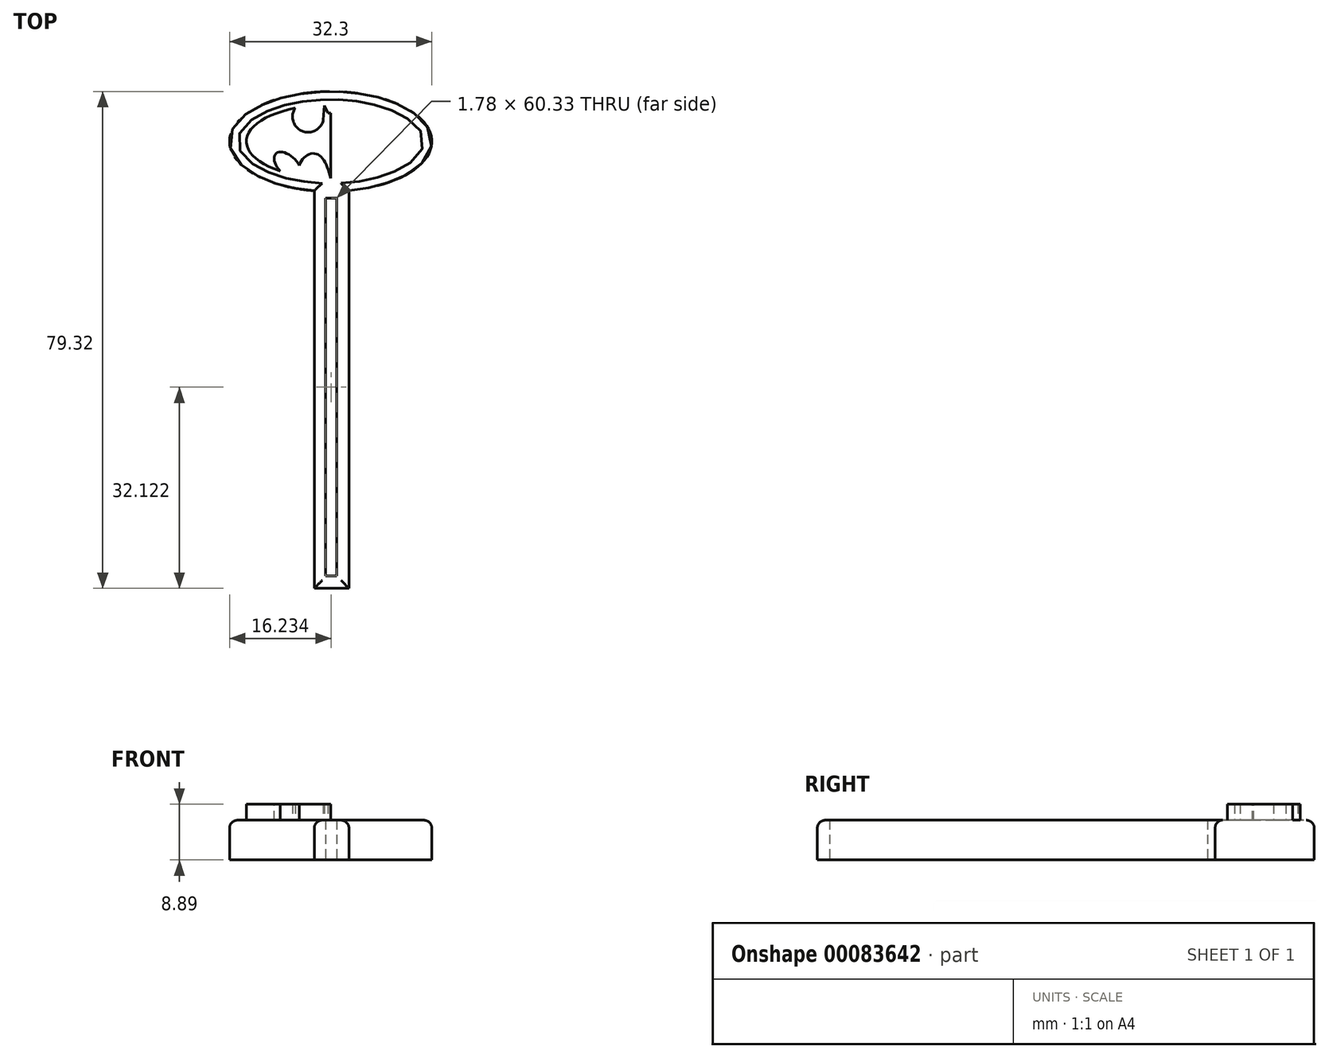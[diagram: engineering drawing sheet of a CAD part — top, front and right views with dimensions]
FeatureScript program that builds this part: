
annotation { "Feature Type Name" : "Feature", "Feature Type Description" : "" }
export const myFeature = defineFeature(function(context is Context, id is Id, definition is map)
    precondition{}
    {
        {
            var Q0;
            Q0=qCreatedBy(makeId("Top.planeOp"),FACE);
            var sketch = newSketch(context, id + "F0", { "sketchPlane" : qUnion([Q0])});
            skLineSegment(sketch, "E0.bottom", {"start": v(-8.05, 29.3) * mm, "end": v(-6.28, 29.3) * mm});
            skLineSegment(sketch, "E0.top", {"start": v(-8.05, -31.02) * mm, "end": v(-6.28, -31.02) * mm});
            skLineSegment(sketch, "E0.left", {"start": v(-8.05, 29.3) * mm, "end": v(-8.05, -31.02) * mm});
            skLineSegment(sketch, "E0.right", {"start": v(-6.28, 29.3) * mm, "end": v(-6.28, -31.02) * mm});
            skLineSegment(sketch, "E1.top", {"start": v(-9.87, -32.98) * mm, "end": v(-4.33, -32.98) * mm});
            skLineSegment(sketch, "E1.left", {"start": v(-9.87, 30.52) * mm, "end": v(-9.87, -32.98) * mm});
            skLineSegment(sketch, "E1.right", {"start": v(-4.33, 30.52) * mm, "end": v(-4.33, -32.98) * mm});
            skEllipticalArc(sketch, "E2", {});
            skPoint(sketch, "E3.startSnap0", {"position": v(-7.25, 46.34) * mm});
            skPoint(sketch, "E3.start.orphan", {"position": v(-7.25, 51.5) * mm});
            const initialGuessF0  = {"E2": [-0.007252356503158808, 0.03836836293339729, 1, 0, 0.016150043811649084, 0.007975973144719452, 4.894343702648654, 4.54976842266986]};
            skSetInitialGuess(sketch, initialGuessF0);
            skSolve(sketch);
        }
        {
            var Q0;
            Q0 = qSketchRegion(id + "F0", true);
            extrude(context, id + "F1", {"entities" : qUnion([Q0]), "depth" : 6.35 * mm});
        }
        {
            var Q0;
            Q0=makeQuery(id+"F1.opExtrude","CAP_FACE",FACE,{"disambiguationData":[OSD([sQuery(id+"F0.wireOp",EDGE,"E0.bottom"),sQuery(id+"F0.wireOp",EDGE,"E0.top"),sQuery(id+"F0.wireOp",EDGE,"E0.left"),sQuery(id+"F0.wireOp",EDGE,"E0.right"),sQuery(id+"F0.wireOp",EDGE,"E1.top"),sQuery(id+"F0.wireOp",EDGE,"E1.left"),sQuery(id+"F0.wireOp",EDGE,"E1.right"),sQuery(id+"F0.wireOp",EDGE,"E2")])],"isStart":false});
            var sketch = newSketch(context, id + "F2", { "sketchPlane" : qUnion([Q0])});
            skEllipticalArc(sketch, "E4", {});
            skLineSegment(sketch, "E5", {"start": v(-7.25, 48.68) * mm, "end": v(-7.25, 32.47) * mm});
            skPoint(sketch, "E5.endSnap0", {"position": v(-7.25, 30.4) * mm});
            skLineSegment(sketch, "E6", {"start": v(-7.25, 42.88) * mm, "end": v(-6.79, 42.88) * mm});
            skPoint(sketch, "E7.first.point", {"position": v(-5.08, 42) * mm});
            skPoint(sketch, "E7.second.point", {"position": v(-1.6, 43.72) * mm});
            skPoint(sketch, "E7.third.point", {"position": v(-3.3, 39.92) * mm});
            skEllipticalArc(sketch, "E8", {});
            skFitSpline(sketch, "E9", {"points": [v(-7.25, 32.47) * mm, v(-4.78, 36.44) * mm, v(-2.26, 34.55) * mm], "startDerivative": vector(2.36, 11.13) * mm, "endDerivative": vector(2.41, -8.56) * mm});
            skEllipticalArc(sketch, "E10.trimOffspring", {});
            skPoint(sketch, "E11.trimOffspring.end.orphan", {"position": v(-7.25, 29.75) * mm});
            skLineSegment(sketch, "E12.MirrorCS", {"start": v(-7.25, 42.88) * mm, "end": v(-7.72, 42.88) * mm});
            skEllipticalArc(sketch, "E13.MirrorCS", {});
            skFitSpline(sketch, "E14.MirrorCS", {"points": [v(-7.25, 32.47) * mm, v(-9.73, 36.44) * mm, v(-12.25, 34.55) * mm], "startDerivative": vector(-2.36, 11.13) * mm, "endDerivative": vector(-2.41, -8.56) * mm});
            skLineSegment(sketch, "E15", {"start": v(-6.79, 42.88) * mm, "end": v(-6.26, 44.13) * mm});
            skLineSegment(sketch, "E16", {"start": v(-6.26, 44.13) * mm, "end": v(-6.07, 41.8) * mm});
            skArc(sketch, "E17", {"start": v(-6.07, 41.8) * mm, "mid": v(-2.67, 40.04) * mm, "end": v(-1.6, 43.72) * mm});
            skPoint(sketch, "E17.third.point", {"position": v(-2.29, 40.25) * mm});
            skLineSegment(sketch, "E18.MirrorCS", {"start": v(-7.72, 42.88) * mm, "end": v(-8.25, 44.13) * mm});
            skLineSegment(sketch, "E19.MirrorCS", {"start": v(-8.25, 44.13) * mm, "end": v(-8.43, 41.8) * mm});
            skArc(sketch, "E20.MirrorCS", {"start": v(-8.43, 41.8) * mm, "mid": v(-11.83, 40.04) * mm, "end": v(-12.9, 43.72) * mm});
            const initialGuessF2  = {"E4": [-0.007252356503158808, 0.03836836293339729, 1, 0, 0.013452716371891214, 0.0058950630208120984, 5.355480264337791, 1.137223244960225], "E8": [-0.00042749958811327815, 0.03451338782906532, 0.7071070265716229, 0.7071065358013869, 0.002727908301320936, 0.0014921496315674547, 4.811673716025654, 2.054311453161399], "E10.trimOffspring": [-0.007252356503158808, 0.03836836293339729, 1, 0, 0.013452716371891214, 0.0058950630208120984, 2.0043694086295685, 4.069297696431589], "E13.MirrorCS": [-0.014078464221015828, 0.034509578750198666, -0.7071070265716227, 0.7071065358013872, 0.002727908301320936, 0.0014921496315674547, 4.228873854018188, 1.4715115911539325]};
            skSetInitialGuess(sketch, initialGuessF2);
            skSolve(sketch);
        }
        {
            var Q0;
            Q0 = qSketchRegion(id + "F2", true);
            extrude(context, id + "F3", {"entities" : qUnion([Q0]), "depth" : 2.54 * mm});
        }
        {
            var Q0;
            Q0=makeQuery(id+"F1.opExtrude","CAP_EDGE",EDGE,{"disambiguationData":[OSD([sQuery(id+"F0.wireOp",EDGE,"E2")])],"isStart":false});
            fillet(context, id + "F4", {"entities" : qUnion([Q0]), "radius" : 1.27 * mm, "tangentPropagation" : true, "allowEdgeOverflow" : false});
        }
        {
            var Q0;
            Q0=makeQuery(id+"F1.opExtrude","CAP_EDGE",EDGE,{"disambiguationData":[OSD([sQuery(id+"F0.wireOp",EDGE,"E1.right")])],"isStart":false});
            var Q1;
            Q1=makeQuery(id+"F1.opExtrude","CAP_EDGE",EDGE,{"disambiguationData":[OSD([sQuery(id+"F0.wireOp",EDGE,"E1.left")])],"isStart":false});
            var Q2;
            Q2=makeQuery(id+"F1.opExtrude","CAP_EDGE",EDGE,{"disambiguationData":[OSD([sQuery(id+"F0.wireOp",EDGE,"E1.top")])],"isStart":false});
            fillet(context, id + "F5", {"entities" : qUnion([Q0, Q1, Q2]), "radius" : 1.27 * mm, "tangentPropagation" : true, "allowEdgeOverflow" : false});
        }
    });
